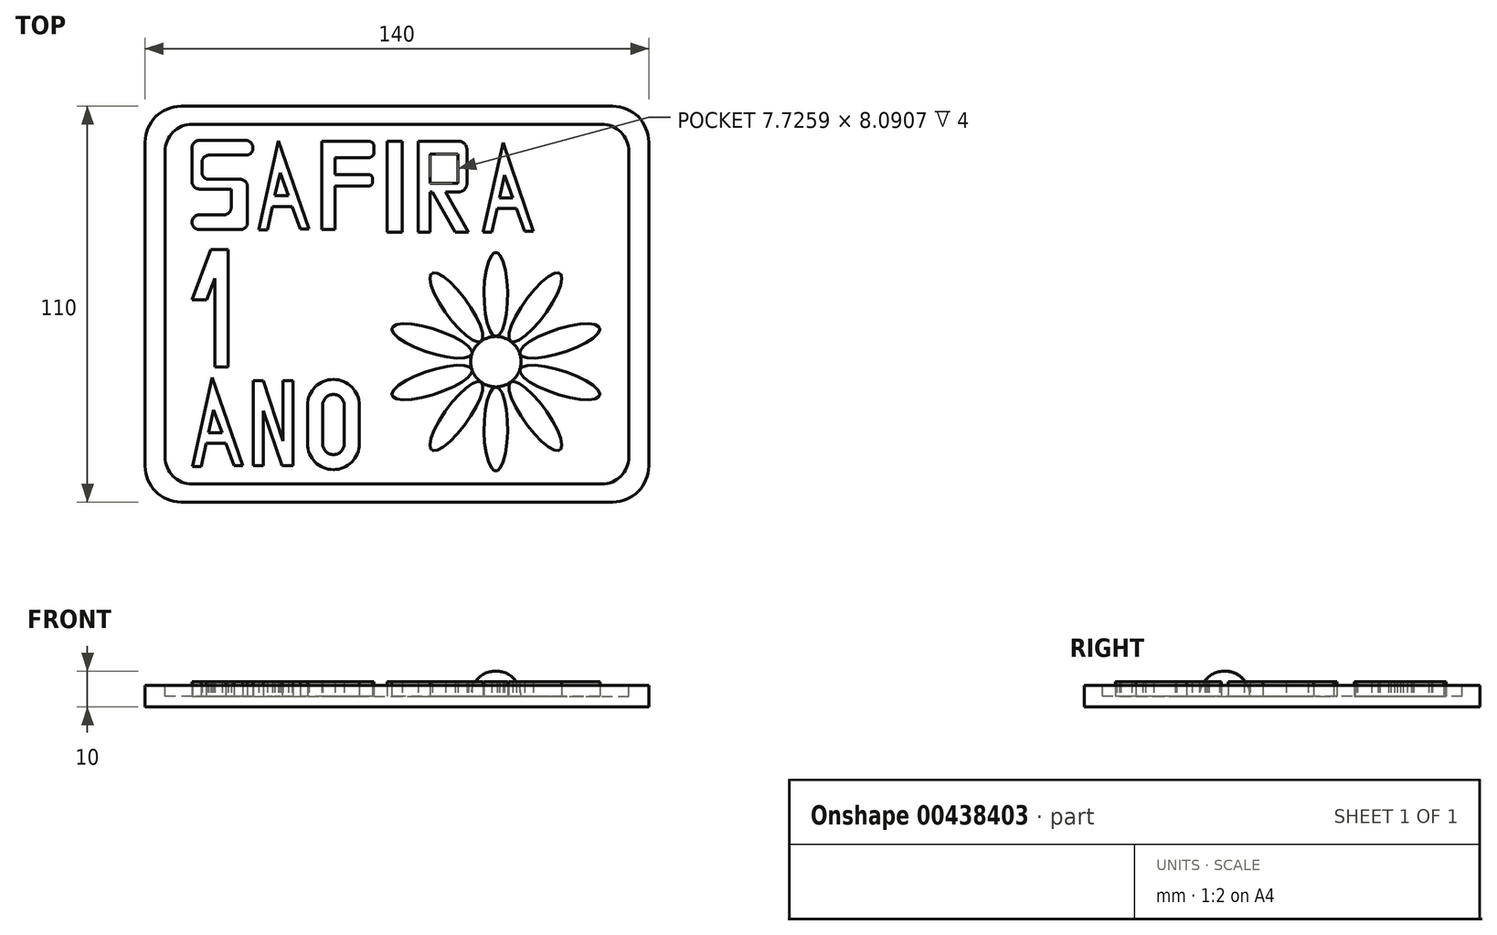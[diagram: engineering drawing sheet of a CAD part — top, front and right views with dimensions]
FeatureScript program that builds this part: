
annotation { "Feature Type Name" : "Feature", "Feature Type Description" : "" }
export const myFeature = defineFeature(function(context is Context, id is Id, definition is map)
    precondition{}
    {
        {
            var Q0;
            Q0=qCreatedBy(makeId("Top.planeOp"),FACE);
            var sketch = newSketch(context, id + "F0", { "sketchPlane" : qUnion([Q0])});
            skLineSegment(sketch, "E0.bottom", {"start": v(-60, -55) * mm, "end": v(60, -55) * mm});
            skLineSegment(sketch, "E0.top", {"start": v(-60, 55) * mm, "end": v(60, 55) * mm});
            skLineSegment(sketch, "E0.left", {"start": v(-70, -45) * mm, "end": v(-70, 45) * mm});
            skLineSegment(sketch, "E0.right", {"start": v(70, -45) * mm, "end": v(70, 45) * mm});
            skPoint(sketch, "E0.middle", {"position": v(0, 0) * mm});
            skPoint(sketch, "E1.visualSharp", {"position": v(70, 55) * mm});
            skArc(sketch, "E1.filletArc", {"start": v(70, 45) * mm, "mid": v(67.07, 52.07) * mm, "end": v(60, 55) * mm});
            skPoint(sketch, "E2.visualSharp", {"position": v(-70, 55) * mm});
            skArc(sketch, "E2.filletArc", {"start": v(-60, 55) * mm, "mid": v(-67.07, 52.07) * mm, "end": v(-70, 45) * mm});
            skPoint(sketch, "E3.visualSharp", {"position": v(-70, -55) * mm});
            skArc(sketch, "E3.filletArc", {"start": v(-70, -45) * mm, "mid": v(-67.07, -52.07) * mm, "end": v(-60, -55) * mm});
            skPoint(sketch, "E4.visualSharp", {"position": v(70, -55) * mm});
            skArc(sketch, "E4.filletArc", {"start": v(60, -55) * mm, "mid": v(67.07, -52.07) * mm, "end": v(70, -45) * mm});
            skSolve(sketch);
        }
        {
            var Q0;
            Q0=makeQuery(id+"F0.imprint","IMPRINT",FACE,{"disambiguationData":[TD([[makeQuery(id+"F0.imprint","IMPRINT",EDGE,{"derivedFrom":sQuery(id+"F0.wireOp",EDGE,"E0.bottom")}),1.0]])]});
            extrude(context, id + "F1", {"entities" : qUnion([Q0]), "depth" : 6 * mm});
        }
        {
            var Q0;
            Q0=makeQuery(id+"F1.opExtrude","CAP_FACE",FACE,{"disambiguationData":[OSD([sQuery(id+"F0.wireOp",EDGE,"E0.bottom"),sQuery(id+"F0.wireOp",EDGE,"E0.top"),sQuery(id+"F0.wireOp",EDGE,"E0.left"),sQuery(id+"F0.wireOp",EDGE,"E0.right"),sQuery(id+"F0.wireOp",EDGE,"E1.filletArc"),sQuery(id+"F0.wireOp",EDGE,"E2.filletArc"),sQuery(id+"F0.wireOp",EDGE,"E3.filletArc"),sQuery(id+"F0.wireOp",EDGE,"E4.filletArc")])],"isStart":false});
            var sketch = newSketch(context, id + "F2", { "sketchPlane" : qUnion([Q0])});
            skLineSegment(sketch, "E5.bottom", {"start": v(-56.94, 50) * mm, "end": v(56.94, 50) * mm});
            skLineSegment(sketch, "E5.top", {"start": v(-56.94, -50) * mm, "end": v(56.94, -50) * mm});
            skLineSegment(sketch, "E5.left", {"start": v(-64.44, 42.5) * mm, "end": v(-64.44, -42.5) * mm});
            skLineSegment(sketch, "E5.right", {"start": v(64.44, 42.5) * mm, "end": v(64.44, -42.5) * mm});
            skPoint(sketch, "E5.middle", {"position": v(0, 0) * mm});
            skPoint(sketch, "E6.visualSharp", {"position": v(-64.44, 50) * mm});
            skArc(sketch, "E6.filletArc", {"start": v(-56.94, 50) * mm, "mid": v(-62.24, 47.8) * mm, "end": v(-64.44, 42.5) * mm});
            skPoint(sketch, "E7.visualSharp", {"position": v(64.44, 50) * mm});
            skArc(sketch, "E7.filletArc", {"start": v(64.44, 42.5) * mm, "mid": v(62.24, 47.8) * mm, "end": v(56.94, 50) * mm});
            skPoint(sketch, "E8.visualSharp", {"position": v(-64.44, -50) * mm});
            skArc(sketch, "E8.filletArc", {"start": v(-64.44, -42.5) * mm, "mid": v(-62.24, -47.8) * mm, "end": v(-56.94, -50) * mm});
            skPoint(sketch, "E9.visualSharp", {"position": v(64.44, -50) * mm});
            skArc(sketch, "E9.filletArc", {"start": v(56.94, -50) * mm, "mid": v(62.24, -47.8) * mm, "end": v(64.44, -42.5) * mm});
            skSolve(sketch);
        }
        {
            var Q0;
            Q0=makeQuery(id+"F2.imprint","IMPRINT",FACE,{"disambiguationData":[TD([[makeQuery(id+"F2.imprint","IMPRINT",EDGE,{"derivedFrom":sQuery(id+"F2.wireOp",EDGE,"E5.bottom")}),-1.0]])]});
            extrude(context, id + "F3", {"entities" : qUnion([Q0]), "operationType" : NewBodyOperationType.REMOVE, "oppositeDirection" : true, "depth" : 3 * mm});
        }
        {
            var Q0;
            Q0=makeQuery(id+"F3.boolean.opBoolean","COPY",FACE,{"derivedFrom":makeQuery(id+"F3.opExtrude","CAP_FACE",FACE,{"disambiguationData":[OSD([sQuery(id+"F2.wireOp",EDGE,"E5.bottom"),sQuery(id+"F2.wireOp",EDGE,"E5.top"),sQuery(id+"F2.wireOp",EDGE,"E5.left"),sQuery(id+"F2.wireOp",EDGE,"E5.right"),sQuery(id+"F2.wireOp",EDGE,"E6.filletArc"),sQuery(id+"F2.wireOp",EDGE,"E7.filletArc"),sQuery(id+"F2.wireOp",EDGE,"E8.filletArc"),sQuery(id+"F2.wireOp",EDGE,"E9.filletArc")])],"isStart":false})});
            var sketch = newSketch(context, id + "F4", { "sketchPlane" : qUnion([Q0])});
            skLineSegment(sketch, "E10", {"start": v(-52.72, 47.46) * mm, "end": v(-52.83, 47.46) * mm});
            skLineSegment(sketch, "E11", {"start": v(-56.94, 42.5) * mm, "end": v(-56.94, 36.3) * mm});
            skLineSegment(sketch, "E12", {"start": v(-56.94, 36.3) * mm, "end": v(-56.94, 34) * mm});
            skLineSegment(sketch, "E13", {"start": v(-54.94, 32) * mm, "end": v(-46.07, 32) * mm});
            skLineSegment(sketch, "E14", {"start": v(-46.07, 32) * mm, "end": v(-46.07, 26.82) * mm});
            skLineSegment(sketch, "E15", {"start": v(-48.07, 24.82) * mm, "end": v(-54.94, 24.82) * mm});
            skLineSegment(sketch, "E16", {"start": v(-56.94, 22.82) * mm, "end": v(-56.94, 22.72) * mm});
            skLineSegment(sketch, "E17", {"start": v(-54.94, 20.72) * mm, "end": v(-43.56, 20.72) * mm});
            skLineSegment(sketch, "E18", {"start": v(-41.56, 22.72) * mm, "end": v(-41.56, 32.69) * mm});
            skLineSegment(sketch, "E19", {"start": v(-40.01, 43.42) * mm, "end": v(-40.01, 43.52) * mm});
            skLineSegment(sketch, "E20", {"start": v(-42.01, 45.52) * mm, "end": v(-54.94, 45.52) * mm});
            skLineSegment(sketch, "E21", {"start": v(-56.94, 43.52) * mm, "end": v(-56.94, 42.5) * mm});
            skLineSegment(sketch, "E22", {"start": v(-42.01, 41.42) * mm, "end": v(-52.2, 41.42) * mm});
            skLineSegment(sketch, "E23", {"start": v(-54.2, 39.42) * mm, "end": v(-54.2, 36.69) * mm});
            skPoint(sketch, "E24.orphan", {"position": v(-41.56, 36.3) * mm});
            skLineSegment(sketch, "E25", {"start": v(-43.56, 34.69) * mm, "end": v(-52.2, 34.69) * mm});
            skLineSegment(sketch, "E26", {"start": v(-38.37, 20.63) * mm, "end": v(-32.9, 45.45) * mm});
            skLineSegment(sketch, "E27", {"start": v(-32.9, 45.45) * mm, "end": v(-24.5, 20.9) * mm});
            skLineSegment(sketch, "E28", {"start": v(-24.5, 20.9) * mm, "end": v(-26.84, 20.9) * mm});
            skLineSegment(sketch, "E29", {"start": v(-38.37, 20.63) * mm, "end": v(-36, 20.63) * mm});
            skLineSegment(sketch, "E30", {"start": v(-32.5, 36.5) * mm, "end": v(-30.2, 30.13) * mm});
            skLineSegment(sketch, "E31", {"start": v(-32.5, 36.5) * mm, "end": v(-33.91, 30.13) * mm});
            skLineSegment(sketch, "E32", {"start": v(-33.91, 30.13) * mm, "end": v(-30.2, 30.13) * mm});
            skLineSegment(sketch, "E33.trimOffspring", {"start": v(-34.58, 27.1) * mm, "end": v(-36, 20.63) * mm});
            skLineSegment(sketch, "E34.trimOffspring", {"start": v(-29.1, 27.1) * mm, "end": v(-26.84, 20.9) * mm});
            skLineSegment(sketch, "E35", {"start": v(-20.94, 45.32) * mm, "end": v(-20.94, 20.71) * mm});
            skLineSegment(sketch, "E36", {"start": v(-20.94, 20.71) * mm, "end": v(-17.16, 20.71) * mm});
            skLineSegment(sketch, "E37", {"start": v(-17.16, 20.71) * mm, "end": v(-17.16, 29.6) * mm});
            skLineSegment(sketch, "E38", {"start": v(-17.16, 29.6) * mm, "end": v(-17.16, 32.88) * mm});
            skLineSegment(sketch, "E39", {"start": v(-17.16, 32.88) * mm, "end": v(-7.65, 32.88) * mm});
            skLineSegment(sketch, "E40", {"start": v(-6.85, 33.68) * mm, "end": v(-6.85, 35.16) * mm});
            skLineSegment(sketch, "E41", {"start": v(-7.65, 35.96) * mm, "end": v(-17.16, 35.96) * mm});
            skLineSegment(sketch, "E42", {"start": v(-17.16, 35.96) * mm, "end": v(-17.16, 40.73) * mm});
            skLineSegment(sketch, "E43", {"start": v(-17.16, 40.73) * mm, "end": v(-7.85, 40.73) * mm});
            skLineSegment(sketch, "E44", {"start": v(-6.35, 42.23) * mm, "end": v(-6.35, 43.82) * mm});
            skLineSegment(sketch, "E45", {"start": v(-7.85, 45.32) * mm, "end": v(-20.94, 45.32) * mm});
            skLineSegment(sketch, "E46", {"start": v(-2.7, 45.28) * mm, "end": v(-2.7, 20) * mm});
            skLineSegment(sketch, "E47", {"start": v(-2.7, 20) * mm, "end": v(1.43, 20) * mm});
            skLineSegment(sketch, "E48", {"start": v(1.43, 45.28) * mm, "end": v(-2.7, 45.28) * mm});
            skLineSegment(sketch, "E49", {"start": v(1.43, 45.28) * mm, "end": v(1.43, 20) * mm});
            skLineSegment(sketch, "E50", {"start": v(5.88, 45.32) * mm, "end": v(5.88, 20) * mm});
            skPoint(sketch, "E50.startSnap0", {"position": v(-13.65, 45.32) * mm});
            skLineSegment(sketch, "E51", {"start": v(5.88, 20) * mm, "end": v(9.26, 20) * mm});
            skLineSegment(sketch, "E52", {"start": v(9.26, 20) * mm, "end": v(9.26, 31.15) * mm});
            skLineSegment(sketch, "E53", {"start": v(9.85, 31.15) * mm, "end": v(16.24, 20) * mm});
            skLineSegment(sketch, "E54", {"start": v(16.24, 20) * mm, "end": v(19.93, 20) * mm});
            skLineSegment(sketch, "E55", {"start": v(19.93, 20) * mm, "end": v(13.53, 31.15) * mm});
            skPoint(sketch, "E55.endSnap0", {"position": v(14.19, 33.76) * mm});
            skLineSegment(sketch, "E56", {"start": v(19.49, 42.82) * mm, "end": v(19.49, 33.65) * mm});
            skLineSegment(sketch, "E57", {"start": v(24, 20.02) * mm, "end": v(29.47, 44.85) * mm});
            skLineSegment(sketch, "E58", {"start": v(29.47, 44.85) * mm, "end": v(37.87, 20.3) * mm});
            skLineSegment(sketch, "E59", {"start": v(37.87, 20.3) * mm, "end": v(35.53, 20.3) * mm});
            skLineSegment(sketch, "E60", {"start": v(24, 20.02) * mm, "end": v(26.36, 20.02) * mm});
            skLineSegment(sketch, "E61", {"start": v(29.86, 35.88) * mm, "end": v(32.17, 29.52) * mm});
            skLineSegment(sketch, "E62", {"start": v(29.86, 35.88) * mm, "end": v(28.46, 29.52) * mm});
            skLineSegment(sketch, "E63", {"start": v(28.46, 29.52) * mm, "end": v(32.17, 29.52) * mm});
            skLineSegment(sketch, "E64.trimOffspring", {"start": v(27.83, 26.66) * mm, "end": v(26.36, 20.02) * mm});
            skLineSegment(sketch, "E65.trimOffspring", {"start": v(33.22, 26.66) * mm, "end": v(35.53, 20.3) * mm});
            skPoint(sketch, "E66.visualSharp", {"position": v(-40.01, 45.52) * mm});
            skArc(sketch, "E66.filletArc", {"start": v(-40.01, 43.52) * mm, "mid": v(-40.6, 44.93) * mm, "end": v(-42.01, 45.52) * mm});
            skPoint(sketch, "E67.visualSharp", {"position": v(-40.01, 41.42) * mm});
            skArc(sketch, "E67.filletArc", {"start": v(-42.01, 41.42) * mm, "mid": v(-40.6, 42) * mm, "end": v(-40.01, 43.42) * mm});
            skPoint(sketch, "E68.visualSharp", {"position": v(-56.94, 45.52) * mm});
            skArc(sketch, "E68.filletArc", {"start": v(-54.94, 45.52) * mm, "mid": v(-56.35, 44.93) * mm, "end": v(-56.94, 43.52) * mm});
            skPoint(sketch, "E69.visualSharp", {"position": v(-56.94, 32) * mm});
            skArc(sketch, "E69.filletArc", {"start": v(-56.94, 34) * mm, "mid": v(-56.35, 32.58) * mm, "end": v(-54.94, 32) * mm});
            skPoint(sketch, "E70.visualSharp", {"position": v(-54.2, 34.69) * mm});
            skArc(sketch, "E70.filletArc", {"start": v(-54.2, 36.69) * mm, "mid": v(-53.62, 35.27) * mm, "end": v(-52.2, 34.69) * mm});
            skPoint(sketch, "E71.visualSharp", {"position": v(-41.56, 34.69) * mm});
            skArc(sketch, "E71.filletArc", {"start": v(-41.56, 32.69) * mm, "mid": v(-42.15, 34.1) * mm, "end": v(-43.56, 34.69) * mm});
            skPoint(sketch, "E72.visualSharp", {"position": v(-56.94, 24.82) * mm});
            skArc(sketch, "E72.filletArc", {"start": v(-54.94, 24.82) * mm, "mid": v(-56.35, 24.24) * mm, "end": v(-56.94, 22.82) * mm});
            skPoint(sketch, "E73.visualSharp", {"position": v(-56.94, 20.72) * mm});
            skArc(sketch, "E73.filletArc", {"start": v(-56.94, 22.72) * mm, "mid": v(-56.35, 21.31) * mm, "end": v(-54.94, 20.72) * mm});
            skPoint(sketch, "E74.visualSharp", {"position": v(-41.56, 20.72) * mm});
            skArc(sketch, "E74.filletArc", {"start": v(-43.56, 20.72) * mm, "mid": v(-42.15, 21.31) * mm, "end": v(-41.56, 22.72) * mm});
            skPoint(sketch, "E75.visualSharp", {"position": v(-54.2, 41.42) * mm});
            skArc(sketch, "E75.filletArc", {"start": v(-52.2, 41.42) * mm, "mid": v(-53.62, 40.83) * mm, "end": v(-54.2, 39.42) * mm});
            skPoint(sketch, "E76.visualSharp", {"position": v(-46.07, 24.82) * mm});
            skArc(sketch, "E76.filletArc", {"start": v(-48.07, 24.82) * mm, "mid": v(-46.65, 25.4) * mm, "end": v(-46.07, 26.82) * mm});
            skPoint(sketch, "E77.visualSharp", {"position": v(-6.85, 35.96) * mm});
            skArc(sketch, "E77.filletArc", {"start": v(-6.85, 35.16) * mm, "mid": v(-7.08, 35.72) * mm, "end": v(-7.65, 35.96) * mm});
            skPoint(sketch, "E78.visualSharp", {"position": v(-6.85, 32.88) * mm});
            skArc(sketch, "E78.filletArc", {"start": v(-7.65, 32.88) * mm, "mid": v(-7.08, 33.11) * mm, "end": v(-6.85, 33.68) * mm});
            skPoint(sketch, "E79.visualSharp", {"position": v(-6.35, 45.32) * mm});
            skArc(sketch, "E79.filletArc", {"start": v(-6.35, 43.82) * mm, "mid": v(-6.8, 44.88) * mm, "end": v(-7.85, 45.32) * mm});
            skPoint(sketch, "E80.visualSharp", {"position": v(-6.35, 40.73) * mm});
            skArc(sketch, "E80.filletArc", {"start": v(-7.85, 40.73) * mm, "mid": v(-6.8, 41.17) * mm, "end": v(-6.35, 42.23) * mm});
            skLineSegment(sketch, "E81.trimOffspring", {"start": v(9.26, 33.65) * mm, "end": v(9.26, 41.74) * mm});
            skPoint(sketch, "E82.visualSharp", {"position": v(19.49, 45.32) * mm});
            skArc(sketch, "E82.filletArc", {"start": v(19.49, 42.82) * mm, "mid": v(18.75, 44.59) * mm, "end": v(16.99, 45.32) * mm});
            skPoint(sketch, "E83.visualSharp", {"position": v(19.49, 31.15) * mm});
            skArc(sketch, "E83.filletArc", {"start": v(16.94, 31.15) * mm, "mid": v(18.74, 31.86) * mm, "end": v(19.49, 33.65) * mm});
            skLineSegment(sketch, "E84", {"start": v(5.88, 45.32) * mm, "end": v(16.99, 45.32) * mm});
            skLineSegment(sketch, "E85", {"start": v(9.26, 41.74) * mm, "end": v(16.99, 41.74) * mm});
            skLineSegment(sketch, "E86", {"start": v(16.99, 41.74) * mm, "end": v(16.99, 33.65) * mm});
            skLineSegment(sketch, "E87", {"start": v(16.99, 33.65) * mm, "end": v(9.26, 33.65) * mm});
            skLineSegment(sketch, "E88", {"start": v(16.94, 31.15) * mm, "end": v(13.53, 31.15) * mm});
            skLineSegment(sketch, "E89.trimOffspring", {"start": v(9.85, 31.15) * mm, "end": v(9.26, 31.15) * mm});
            skLineSegment(sketch, "E90", {"start": v(-46.87, 15.18) * mm, "end": v(-46.87, -17.5) * mm});
            skLineSegment(sketch, "E91", {"start": v(-46.87, -17.5) * mm, "end": v(-50.67, -17.5) * mm});
            skLineSegment(sketch, "E92", {"start": v(-50.67, -17.5) * mm, "end": v(-50.67, 7.16) * mm});
            skLineSegment(sketch, "E93", {"start": v(-46.87, 15.18) * mm, "end": v(-50.67, 15.18) * mm});
            skLineSegment(sketch, "E94", {"start": v(-55.12, 1.15) * mm, "end": v(-52.92, 1.15) * mm});
            skLineSegment(sketch, "E95", {"start": v(-52.92, 1.15) * mm, "end": v(-50.67, 7.16) * mm});
            skLineSegment(sketch, "E96", {"start": v(-34.58, 27.1) * mm, "end": v(-29.1, 27.1) * mm});
            skLineSegment(sketch, "E97", {"start": v(27.83, 26.66) * mm, "end": v(32.75, 26.66) * mm});
            skLineSegment(sketch, "E98", {"start": v(32.75, 26.66) * mm, "end": v(33.22, 26.66) * mm});
            skLineSegment(sketch, "E99", {"start": v(-56.8, -45.2) * mm, "end": v(-51.32, -20.38) * mm});
            skLineSegment(sketch, "E100", {"start": v(-51.32, -20.38) * mm, "end": v(-42.92, -44.93) * mm});
            skLineSegment(sketch, "E101", {"start": v(-42.92, -44.93) * mm, "end": v(-45.26, -44.93) * mm});
            skLineSegment(sketch, "E102", {"start": v(-56.8, -45.2) * mm, "end": v(-54.43, -45.2) * mm});
            skLineSegment(sketch, "E103", {"start": v(-50.93, -29.34) * mm, "end": v(-48.62, -35.7) * mm});
            skLineSegment(sketch, "E104", {"start": v(-50.93, -29.34) * mm, "end": v(-52.33, -35.7) * mm});
            skLineSegment(sketch, "E105", {"start": v(-52.33, -35.7) * mm, "end": v(-48.62, -35.7) * mm});
            skLineSegment(sketch, "E106.trimOffspring", {"start": v(-53, -38.73) * mm, "end": v(-54.43, -45.2) * mm});
            skLineSegment(sketch, "E107.trimOffspring", {"start": v(-47.52, -38.73) * mm, "end": v(-45.26, -44.93) * mm});
            skLineSegment(sketch, "E108", {"start": v(-53, -38.73) * mm, "end": v(-47.52, -38.73) * mm});
            skLineSegment(sketch, "E109", {"start": v(-39.96, -44.96) * mm, "end": v(-39.96, -21.3) * mm});
            skLineSegment(sketch, "E110", {"start": v(-39.96, -21.3) * mm, "end": v(-37.1, -21.3) * mm});
            skLineSegment(sketch, "E111", {"start": v(-28.95, -21.3) * mm, "end": v(-31.7, -21.3) * mm});
            skLineSegment(sketch, "E112", {"start": v(-39.96, -44.96) * mm, "end": v(-37.1, -44.96) * mm});
            skLineSegment(sketch, "E113", {"start": v(-37.1, -44.96) * mm, "end": v(-37.1, -29.71) * mm});
            skLineSegment(sketch, "E114", {"start": v(-28.95, -44.96) * mm, "end": v(-31.92, -44.96) * mm});
            skLineSegment(sketch, "E115", {"start": v(-37.1, -29.71) * mm, "end": v(-31.92, -44.96) * mm});
            skPoint(sketch, "E116.endSnap0", {"position": v(-30.07, -44.96) * mm});
            skLineSegment(sketch, "E117", {"start": v(-31.7, -21.3) * mm, "end": v(-31.7, -38.05) * mm});
            skLineSegment(sketch, "E118", {"start": v(-28.95, -21.3) * mm, "end": v(-28.95, -44.96) * mm});
            skPoint(sketch, "E119.orphan", {"position": v(-28.22, -21.3) * mm});
            skLineSegment(sketch, "E120", {"start": v(-37.1, -21.3) * mm, "end": v(-31.7, -38.05) * mm});
            skArc(sketch, "E121", {"start": v(-19.34, -21.12) * mm, "mid": v(-23.02, -23.33) * mm, "end": v(-24.79, -27.24) * mm});
            skArc(sketch, "E122", {"start": v(-19.34, -21.12) * mm, "mid": v(-13.2, -22.46) * mm, "end": v(-10.46, -28.11) * mm});
            skArc(sketch, "E123", {"start": v(-24.79, -27.24) * mm, "mid": v(-24.83, -27.67) * mm, "end": v(-24.84, -28.11) * mm});
            skArc(sketch, "E124.MirrorCS", {"start": v(-19.34, -45.8) * mm, "mid": v(-13.2, -44.46) * mm, "end": v(-10.46, -38.8) * mm});
            skArc(sketch, "E125.MirrorCS", {"start": v(-24.79, -39.69) * mm, "mid": v(-24.83, -39.25) * mm, "end": v(-24.84, -38.8) * mm});
            skArc(sketch, "E126.MirrorCS", {"start": v(-19.34, -45.8) * mm, "mid": v(-23.02, -43.6) * mm, "end": v(-24.79, -39.69) * mm});
            skLineSegment(sketch, "E127", {"start": v(-24.84, -28.11) * mm, "end": v(-24.84, -38.8) * mm});
            skLineSegment(sketch, "E128", {"start": v(-10.46, -28.11) * mm, "end": v(-10.46, -38.8) * mm});
            skArc(sketch, "E129", {"start": v(-14.65, -28.11) * mm, "mid": v(-17.65, -25.11) * mm, "end": v(-20.65, -28.11) * mm});
            skArc(sketch, "E130", {"start": v(-20.65, -38.8) * mm, "mid": v(-17.65, -41.8) * mm, "end": v(-14.65, -38.8) * mm});
            skLineSegment(sketch, "E131", {"start": v(-20.65, -38.8) * mm, "end": v(-20.65, -28.11) * mm});
            skLineSegment(sketch, "E132", {"start": v(-14.65, -38.8) * mm, "end": v(-14.65, -28.11) * mm});
            skPoint(sketch, "E133.orphan", {"position": v(-22, -37.89) * mm});
            skLineSegment(sketch, "E134", {"start": v(-55.12, 1.15) * mm, "end": v(-56.97, 1.15) * mm});
            skLineSegment(sketch, "E135", {"start": v(-56.97, 1.15) * mm, "end": v(-51.73, 15.18) * mm});
            skLineSegment(sketch, "E136", {"start": v(-50.67, 15.18) * mm, "end": v(-51.73, 15.18) * mm});
            skCircle(sketch, "E137", {"center": v(35.85, -8.83) * mm, "radius": 6 * mm});
            skCircle(sketch, "E138", {"center": v(35.85, -19) * mm, "radius": 3.25 * mm});
            skCircle(sketch, "E139", {"center": v(35.85, -34.04) * mm, "radius": 4 * mm});
            skSolve(sketch);
        }
        {
            var Q0;
            Q0=makeQuery(id+"F4.imprint","IMPRINT",FACE,{"disambiguationData":[TD([[makeQuery(id+"F4.imprint","IMPRINT",EDGE,{"derivedFrom":sQuery(id+"F4.wireOp",EDGE,"E11")}),1.0]])]});
            var Q1;
            Q1=makeQuery(id+"F4.imprint","IMPRINT",FACE,{"disambiguationData":[TD([[makeQuery(id+"F4.imprint","IMPRINT",EDGE,{"derivedFrom":sQuery(id+"F4.wireOp",EDGE,"E26")}),-1.0]])]});
            var Q2;
            Q2=makeQuery(id+"F4.imprint","IMPRINT",FACE,{"disambiguationData":[TD([[makeQuery(id+"F4.imprint","IMPRINT",EDGE,{"derivedFrom":sQuery(id+"F4.wireOp",EDGE,"E35")}),1.0]])]});
            var Q3;
            Q3=makeQuery(id+"F4.imprint","IMPRINT",FACE,{"disambiguationData":[TD([[makeQuery(id+"F4.imprint","IMPRINT",EDGE,{"derivedFrom":sQuery(id+"F4.wireOp",EDGE,"E46")}),1.0]])]});
            var Q4;
            Q4=makeQuery(id+"F4.imprint","IMPRINT",FACE,{"disambiguationData":[TD([[makeQuery(id+"F4.imprint","IMPRINT",EDGE,{"derivedFrom":sQuery(id+"F4.wireOp",EDGE,"E50")}),1.0]])]});
            var Q5;
            Q5=makeQuery(id+"F4.imprint","IMPRINT",FACE,{"disambiguationData":[TD([[makeQuery(id+"F4.imprint","IMPRINT",EDGE,{"derivedFrom":sQuery(id+"F4.wireOp",EDGE,"E57")}),-1.0]])]});
            var Q6;
            Q6=makeQuery(id+"F4.imprint","IMPRINT",FACE,{"disambiguationData":[TD([[makeQuery(id+"F4.imprint","IMPRINT",EDGE,{"derivedFrom":sQuery(id+"F4.wireOp",EDGE,"E90")}),-1.0]])]});
            var Q7;
            Q7=makeQuery(id+"F4.imprint","IMPRINT",FACE,{"disambiguationData":[TD([[makeQuery(id+"F4.imprint","IMPRINT",EDGE,{"derivedFrom":sQuery(id+"F4.wireOp",EDGE,"E99")}),-1.0]])]});
            var Q8;
            Q8=makeQuery(id+"F4.imprint","IMPRINT",FACE,{"disambiguationData":[TD([[makeQuery(id+"F4.imprint","IMPRINT",EDGE,{"derivedFrom":sQuery(id+"F4.wireOp",EDGE,"E109")}),-1.0]])]});
            var Q9;
            Q9=makeQuery(id+"F4.imprint","IMPRINT",FACE,{"disambiguationData":[TD([[makeQuery(id+"F4.imprint","IMPRINT",EDGE,{"derivedFrom":sQuery(id+"F4.wireOp",EDGE,"E121")}),1.0]])]});
            extrude(context, id + "F5", {"entities" : qUnion([Q0, Q1, Q2, Q3, Q4, Q5, Q6, Q7, Q8, Q9]), "operationType" : NewBodyOperationType.ADD, "depth" : 4 * mm});
        }
        {
            var Q0;
            {var subQ0=sQuery(id+"F2.wireOp",EDGE,"E5.right");var subQ1=sQuery(id+"F2.wireOp",EDGE,"E5.left");var subQ2=sQuery(id+"F2.wireOp",EDGE,"E5.top");var subQ3=sQuery(id+"F2.wireOp",EDGE,"E7.filletArc");var subQ4=sQuery(id+"F2.wireOp",EDGE,"E8.filletArc");var subQ5=sQuery(id+"F2.wireOp",EDGE,"E9.filletArc");var subQ6=sQuery(id+"F2.wireOp",EDGE,"E6.filletArc");var subQ7=sQuery(id+"F2.wireOp",EDGE,"E5.bottom");Q0=makeQuery(id+"F5.boolean.opBoolean","SPLIT",FACE,{"disambiguationData":[TD([makeQuery(id+"F3.boolean.opBoolean","COPY",FACE,{"derivedFrom":makeQuery(id+"F3.opExtrude","SWEPT_FACE",FACE,{"disambiguationData":[OSD([subQ7])]})})])],"derivedFrom":makeQuery(id+"F3.boolean.opBoolean","COPY",FACE,{"derivedFrom":makeQuery(id+"F3.opExtrude","CAP_FACE",FACE,{"disambiguationData":[OSD([subQ7,subQ2,subQ1,subQ0,subQ6,subQ3,subQ4,subQ5])],"isStart":false})})});}
            var sketch = newSketch(context, id + "F6", { "sketchPlane" : qUnion([Q0])});
            skSolve(sketch);
        }
        {
            var Q0;
            Q0=qCreatedBy(makeId("Right.planeOp"),FACE);
            cPlane(context, id + "F7", {"entities" : qUnion([Q0]), "cplaneType" : CPlaneType.OFFSET, "offset" : 27.5 * mm, "width" : 150 * mm, "height" : 150 * mm});
        }
        {
            var Q0;
            Q0=qCreatedBy(id+"F7.planeOp",FACE);
            var sketch = newSketch(context, id + "F8", { "sketchPlane" : qUnion([Q0])});
            skLineSegment(sketch, "E140", {"start": v(0, 0) * mm, "end": v(-16, 0) * mm});
            skLineSegment(sketch, "E141", {"start": v(-16, 0) * mm, "end": v(-16, 10) * mm});
            skLineSegment(sketch, "E142", {"start": v(-16, 0) * mm, "end": v(-16, 3) * mm});
            skArc(sketch, "E143", {"start": v(-9, 3) * mm, "mid": v(-11.05, 7.95) * mm, "end": v(-16, 10) * mm});
            skLineSegment(sketch, "E144", {"start": v(-16, 3) * mm, "end": v(-9, 3) * mm});
            skSolve(sketch);
        }
        {
            var Q0;
            Q0=makeQuery(id+"F8.imprint","IMPRINT",FACE,{"disambiguationData":[TD([[makeQuery(id+"F8.imprint","IMPRINT",EDGE,{"derivedFrom":sQuery(id+"F8.wireOp",EDGE,"E141")}),-1.0]])]});
            var Q1;
            Q1=sQuery(id+"F8.wireOp",EDGE,"E142");
            revolve(context, id + "F9", {"operationType" : NewBodyOperationType.ADD, "entities" : qUnion([Q0]), "axis" : qUnion([Q1]), "revolveType" : RevolveType.FULL});
        }
        {
            var Q0;
            Q0=makeQuery(id+"F6.imprint","IMPRINT",FACE,{"disambiguationData":[TD([[makeQuery(id+"F6.imprint","IMPRINT",EDGE,{"derivedFrom":makeQuery(id+"F3.boolean.opBoolean","COPY",EDGE,{"derivedFrom":makeQuery(id+"F3.opExtrude","CAP_EDGE",EDGE,{"disambiguationData":[OSD([sQuery(id+"F2.wireOp",EDGE,"E5.bottom")])],"isStart":false})})}),-1.0]])]});
            var sketch = newSketch(context, id + "F10", { "sketchPlane" : qUnion([Q0])});
            skLineSegment(sketch, "E145", {"start": v(0, 0) * mm, "end": v(27.5, 0) * mm});
            skLineSegment(sketch, "E146", {"start": v(27.5, 0) * mm, "end": v(27.5, -9) * mm});
            skEllipse(sketch, "E147", {"center": v(27.5, 2.68) * mm, "majorRadius": 11.68 * mm, "minorRadius": 3.3 * mm, "majorAxis": v(0, -1)});
            skLineSegment(sketch, "E148", {"start": v(27.5, -9) * mm, "end": v(27.5, -16) * mm});
            skEllipse(sketch, "E149.1.0", {"center": v(16.52, -0.89) * mm, "majorRadius": 11.68 * mm, "minorRadius": 3.3 * mm, "majorAxis": v(0.59, -0.8)});
            skEllipse(sketch, "E149.2.0", {"center": v(9.74, -10.23) * mm, "majorRadius": 11.68 * mm, "minorRadius": 3.3 * mm, "majorAxis": v(0.95, -0.3)});
            skEllipse(sketch, "E149.3.0", {"center": v(9.74, -21.77) * mm, "majorRadius": 11.68 * mm, "minorRadius": 3.3 * mm, "majorAxis": v(0.95, 0.3)});
            skEllipse(sketch, "E149.4.0", {"center": v(16.52, -31.11) * mm, "majorRadius": 11.68 * mm, "minorRadius": 3.3 * mm, "majorAxis": v(0.59, 0.8)});
            skEllipse(sketch, "E149.5.0", {"center": v(27.5, -34.68) * mm, "majorRadius": 11.68 * mm, "minorRadius": 3.3 * mm, "majorAxis": v(0, 1)});
            skEllipse(sketch, "E149.6.0", {"center": v(38.48, -31.11) * mm, "majorRadius": 11.68 * mm, "minorRadius": 3.3 * mm, "majorAxis": v(-0.59, 0.8)});
            skEllipse(sketch, "E149.7.0", {"center": v(45.26, -21.77) * mm, "majorRadius": 11.68 * mm, "minorRadius": 3.3 * mm, "majorAxis": v(-0.95, 0.3)});
            skEllipse(sketch, "E149.8.0", {"center": v(45.26, -10.23) * mm, "majorRadius": 11.68 * mm, "minorRadius": 3.3 * mm, "majorAxis": v(-0.95, -0.3)});
            skEllipse(sketch, "E149.9.0", {"center": v(38.48, -0.89) * mm, "majorRadius": 11.68 * mm, "minorRadius": 3.3 * mm, "majorAxis": v(-0.59, -0.8)});
            skPoint(sketch, "E149.center", {"position": v(27.5, -16) * mm});
            skSolve(sketch);
        }
        {
            var Q0;
            Q0 = qSketchRegion(id + "F10", true);
            extrude(context, id + "F11", {"entities" : qUnion([Q0]), "operationType" : NewBodyOperationType.ADD, "depth" : 4 * mm});
        }
    });
